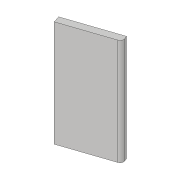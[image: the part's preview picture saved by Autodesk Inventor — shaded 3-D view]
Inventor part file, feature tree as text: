
AUTODESK INVENTOR PART (.ipt)
format: ipt  version: 2018.3 (Build 223284000, 284)  size: 77,824 bytes
history: native  units: in
note: dims shown in document units (in); Inventor stores cm internally (conversion verified against a paired STEP export)
features: extrude x1, fillet x1, sketch x1
ambient origin geometry x8: Origin, YZ Plane, XZ Plane, XY Plane, X Axis, Y Axis, Z Axis, Center Point
bodies: Solid1 (feature_tree)
feature tree (3):
  extrude  "Extrusion1"  Depth=1.925in TaperAngle=0.0deg
  fillet  "Fillet1"  Radius=0.125in
  sketch  "Sketch1"  dims[d0=0.975in d3=1.925in d4=0.0in d5=0.125in d6=0.0625in]
